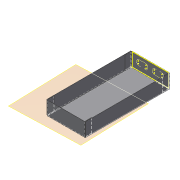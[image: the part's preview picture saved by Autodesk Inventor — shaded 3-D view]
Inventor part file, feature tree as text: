
AUTODESK INVENTOR PART (.ipt)
format: ipt  version: 2015 (Build 190159000, 159)  size: 238,080 bytes
history: native  units: mm
features: reference x24, sheet_metal_op x7, other x5, sketch x5, plane x1, projected_geometry x1
ambient origin geometry x8: Origin, YZ Plane, XZ Plane, XY Plane, X Axis, Y Axis, Z Axis, Center Point
bodies: Solid1 (feature_tree)
feature tree (43):
  plane  "Work Plane1"
  sheet_metal_op  "Face1"
  sheet_metal_op  "Flange1"
  sheet_metal_op  "Flange2"
  other  "A-Side Definition"
  sketch  "Sketch4"  dims[d4=0.9mm]
  sketch  "Sketch5"  dims[d5=0.45mm d6=1.8mm d7=0.9mm d8=40.0mm d9=90.0deg d10=0.9mm d11=3.6mm d12=0.9mm d13=0.9mm d14=0.9mm d15=0.45mm d16=1.8mm d17=0.9mm d18=20.0mm d19=90.0deg d20=0.9mm d21=3.6mm d22=0.9mm d23=0.9mm d25=1.0mm d26=1.0mm]
  sketch  "Sketch1"  dims[d0=240.0mm]
  other  "Plate1"
  sketch  "Sketch2"  dims[d1=110.0mm]
  other  "Plate2"
  sheet_metal_op  "Bend1"
  sheet_metal_op  "Corner1"
  sketch  "Sketch3"  dims[d3=0.9mm]
  other  "Plate3"
  sheet_metal_op  "Bend2"
  sheet_metal_op  "Corner2"
  projected_geometry  "Projected Loop1"
  reference  "Reference1"
  reference  "Reference2"
  reference  "Reference3"
  reference  "Reference4"
  reference  "Reference5"
  reference  "Reference6"
  reference  "Reference7"
  reference  "Reference8"
  reference  "Reference9"
  reference  "Reference10"
  reference  "Reference11"
  reference  "Reference12"
  reference  "Reference13"
  reference  "Reference14"
  reference  "Reference15"
  reference  "Reference16"
  reference  "Reference17"
  reference  "Reference18"
  reference  "Reference19"
  reference  "Reference20"
  reference  "Reference21"
  reference  "Reference22"
  reference  "Reference23"
  reference  "Reference24"
  other  "Definition1"
